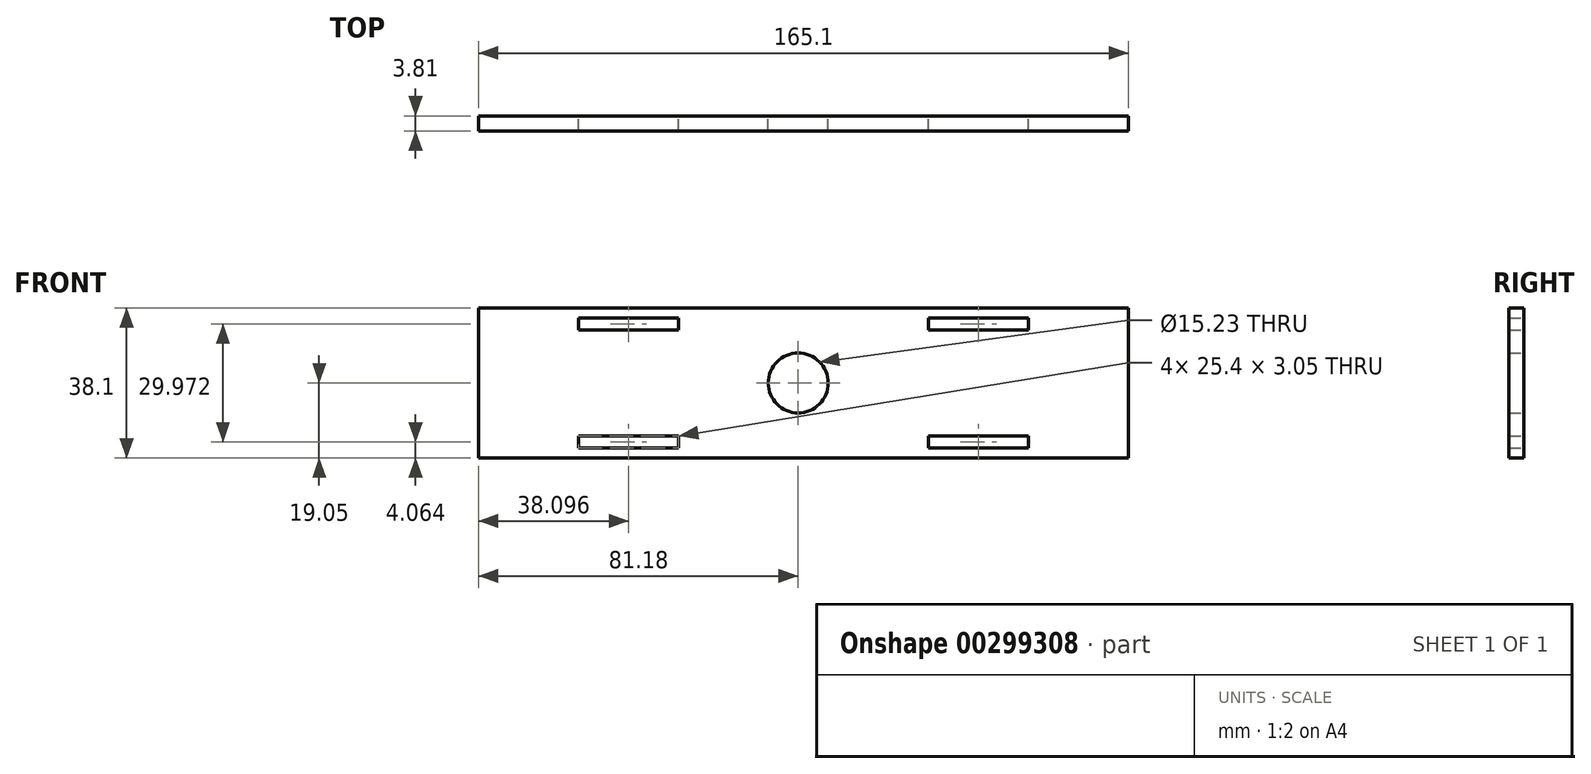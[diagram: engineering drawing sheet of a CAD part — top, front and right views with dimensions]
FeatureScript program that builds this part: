
annotation { "Feature Type Name" : "Feature", "Feature Type Description" : "" }
export const myFeature = defineFeature(function(context is Context, id is Id, definition is map)
    precondition{}
    {
        {
            var Q0;
            Q0=qCreatedBy(makeId("Front.planeOp"),FACE);
            var sketch = newSketch(context, id + "F0", { "sketchPlane" : qUnion([Q0])});
            skLineSegment(sketch, "E0.bottom", {"start": v(-81.18, 38.1) * mm, "end": v(83.92, 38.1) * mm});
            skLineSegment(sketch, "E0.top", {"start": v(-81.18, 0) * mm, "end": v(83.92, 0) * mm});
            skLineSegment(sketch, "E0.left", {"start": v(-81.18, 38.1) * mm, "end": v(-81.18, 0) * mm});
            skLineSegment(sketch, "E0.right", {"start": v(83.92, 38.1) * mm, "end": v(83.92, 0) * mm});
            skLineSegment(sketch, "E1.bottom", {"start": v(-55.78, 5.59) * mm, "end": v(-30.38, 5.59) * mm});
            skLineSegment(sketch, "E1.top", {"start": v(-55.78, 2.54) * mm, "end": v(-30.38, 2.54) * mm});
            skLineSegment(sketch, "E1.left", {"start": v(-55.78, 5.59) * mm, "end": v(-55.78, 2.54) * mm});
            skLineSegment(sketch, "E1.right", {"start": v(-30.38, 5.59) * mm, "end": v(-30.38, 2.54) * mm});
            skLineSegment(sketch, "E2.bottom", {"start": v(33.12, 35.56) * mm, "end": v(58.52, 35.56) * mm});
            skLineSegment(sketch, "E2.top", {"start": v(33.12, 32.51) * mm, "end": v(58.52, 32.51) * mm});
            skLineSegment(sketch, "E2.left", {"start": v(33.12, 35.56) * mm, "end": v(33.12, 32.51) * mm});
            skLineSegment(sketch, "E2.right", {"start": v(58.52, 35.56) * mm, "end": v(58.52, 32.51) * mm});
            skLineSegment(sketch, "E3.bottom", {"start": v(33.12, 5.59) * mm, "end": v(58.52, 5.59) * mm});
            skLineSegment(sketch, "E3.top", {"start": v(33.12, 2.54) * mm, "end": v(58.52, 2.54) * mm});
            skLineSegment(sketch, "E3.left", {"start": v(33.12, 5.59) * mm, "end": v(33.12, 2.54) * mm});
            skLineSegment(sketch, "E3.right", {"start": v(58.52, 5.59) * mm, "end": v(58.52, 2.54) * mm});
            skLineSegment(sketch, "E4.bottom", {"start": v(-55.78, 35.56) * mm, "end": v(-30.38, 35.56) * mm});
            skLineSegment(sketch, "E4.top", {"start": v(-55.78, 32.51) * mm, "end": v(-30.38, 32.51) * mm});
            skLineSegment(sketch, "E4.left", {"start": v(-55.78, 35.56) * mm, "end": v(-55.78, 32.51) * mm});
            skLineSegment(sketch, "E4.right", {"start": v(-30.38, 35.56) * mm, "end": v(-30.38, 32.51) * mm});
            skSolve(sketch);
        }
        {
            var Q0;
            Q0=makeQuery(id+"F0.imprint","IMPRINT",FACE,{"disambiguationData":[TD([[makeQuery(id+"F0.imprint","IMPRINT",EDGE,{"derivedFrom":sQuery(id+"F0.wireOp",EDGE,"E0.bottom")}),-1.0]])]});
            var sketch = newSketch(context, id + "F1", { "sketchPlane" : qUnion([Q0])});
            skCircle(sketch, "E5", {"center": v(0, 19.05) * mm, "radius": 7.62 * mm});
            skSolve(sketch);
        }
        {
            var Q0;
            Q0=makeQuery(id+"F0.imprint","IMPRINT",FACE,{"disambiguationData":[TD([[makeQuery(id+"F0.imprint","IMPRINT",EDGE,{"derivedFrom":sQuery(id+"F0.wireOp",EDGE,"E0.bottom")}),-1.0]])]});
            extrude(context, id + "F2", {"entities" : qUnion([Q0]), "depth" : 3.8 * mm});
        }
        {
            var Q0;
            Q0=makeQuery(id+"F1.imprint","IMPRINT",FACE,{"disambiguationData":[TD([[makeQuery(id+"F1.imprint","IMPRINT",EDGE,{"derivedFrom":sQuery(id+"F1.wireOp",EDGE,"E5")}),1.0]])]});
            extrude(context, id + "F3", {"entities" : qUnion([Q0]), "operationType" : NewBodyOperationType.REMOVE, "depth" : 28.96 * mm});
        }
    });
